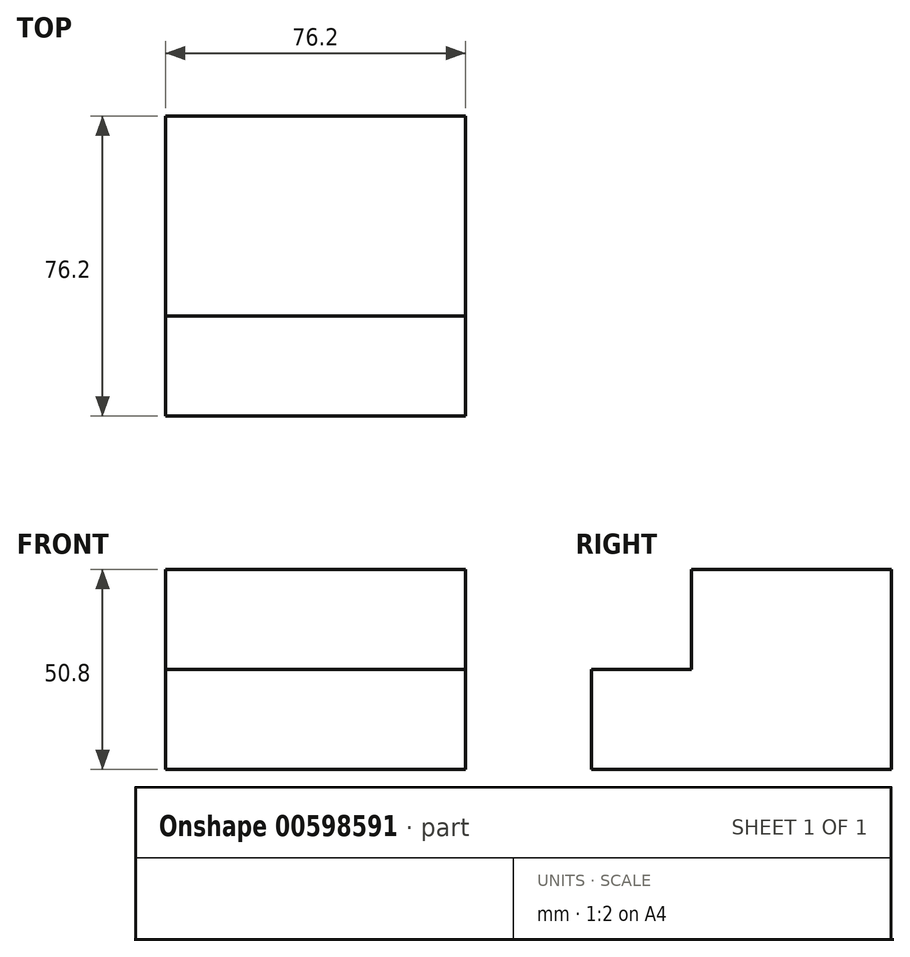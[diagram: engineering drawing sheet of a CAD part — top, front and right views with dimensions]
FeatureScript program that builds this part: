
annotation { "Feature Type Name" : "Feature", "Feature Type Description" : "" }
export const myFeature = defineFeature(function(context is Context, id is Id, definition is map)
    precondition{}
    {
        {
            var Q0;
            Q0=qCreatedBy(makeId("Right.planeOp"),FACE);
            var sketch = newSketch(context, id + "F0", { "sketchPlane" : qUnion([Q0])});
            skLineSegment(sketch, "E0", {"start": v(0, 0) * mm, "end": v(76.2, 0) * mm});
            skLineSegment(sketch, "E1", {"start": v(76.2, 0) * mm, "end": v(76.2, 50.8) * mm});
            skLineSegment(sketch, "E2", {"start": v(76.2, 50.8) * mm, "end": v(25.4, 50.8) * mm});
            skLineSegment(sketch, "E3", {"start": v(25.4, 50.8) * mm, "end": v(25.4, 25.4) * mm});
            skLineSegment(sketch, "E4", {"start": v(25.4, 25.4) * mm, "end": v(0, 25.4) * mm});
            skLineSegment(sketch, "E5", {"start": v(0, 25.4) * mm, "end": v(0, 0) * mm});
            skSolve(sketch);
        }
        {
            var Q0;
            Q0 = qSketchRegion(id + "F0", true);
            extrude(context, id + "F1", {"entities" : qUnion([Q0]), "depth" : 76.2 * mm, "offsetDistance" : 25.4 * mm});
        }
    });
